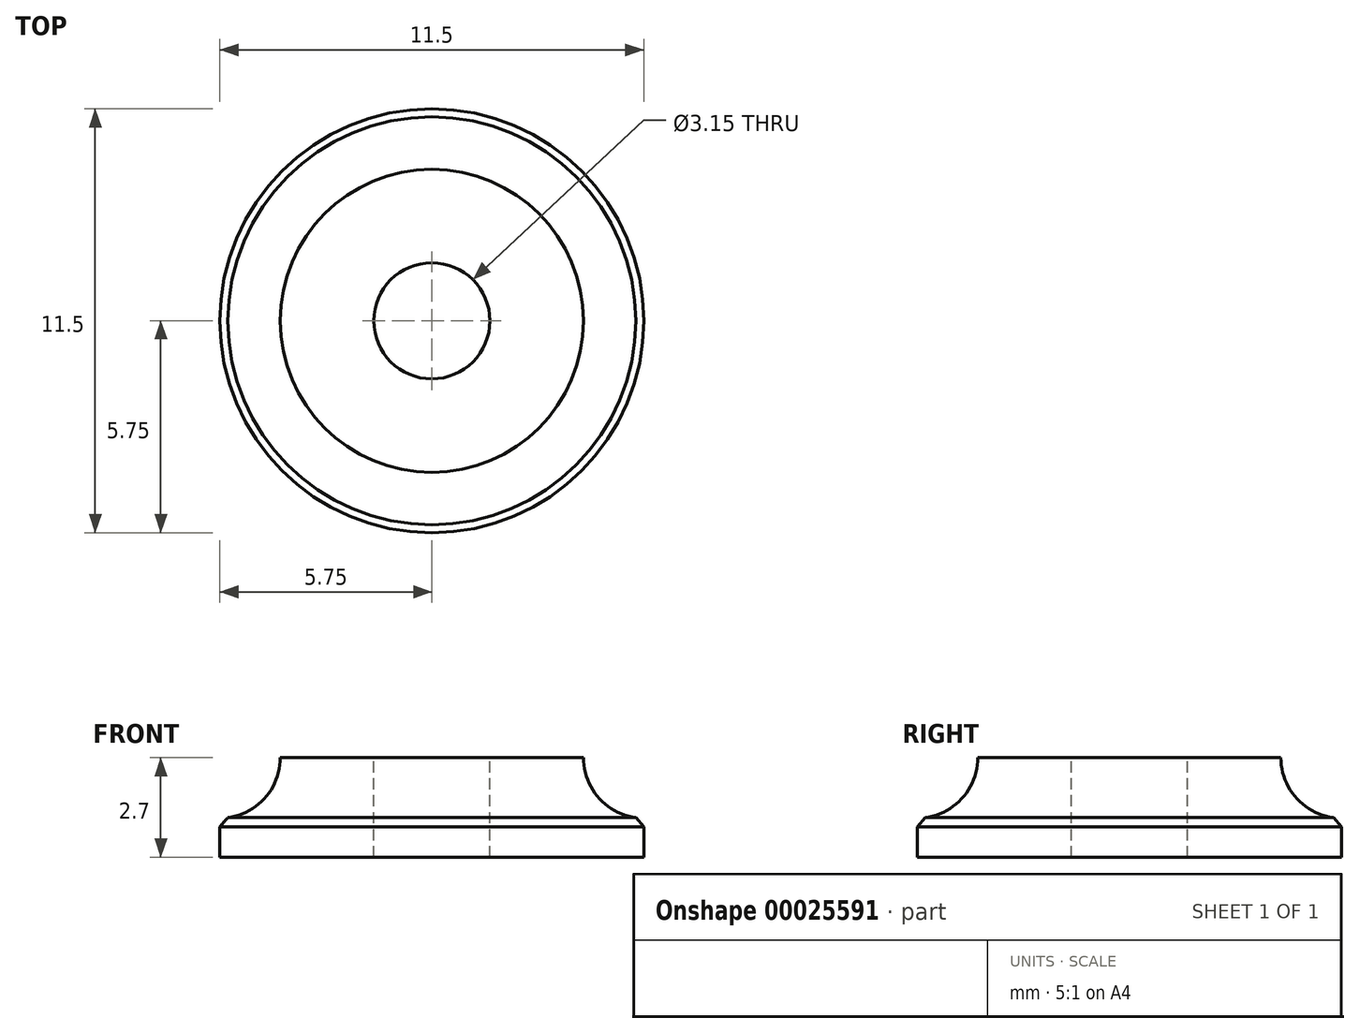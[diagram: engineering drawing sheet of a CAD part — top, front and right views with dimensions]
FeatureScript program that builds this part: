
annotation { "Feature Type Name" : "Feature", "Feature Type Description" : "" }
export const myFeature = defineFeature(function(context is Context, id is Id, definition is map)
    precondition{}
    {
        {
            var Q0;
            Q0=qCreatedBy(makeId("Front.planeOp"),FACE);
            var sketch = newSketch(context, id + "F0", { "sketchPlane" : qUnion([Q0])});
            skLineSegment(sketch, "E0", {"start": v(0, 0) * mm, "end": v(5.75, 0) * mm});
            skLineSegment(sketch, "E1", {"start": v(5.75, 0) * mm, "end": v(5.75, 1.06) * mm});
            skLineSegment(sketch, "E2", {"start": v(0, 0) * mm, "end": v(0, 2.7) * mm});
            skLineSegment(sketch, "E3", {"start": v(0, 2.7) * mm, "end": v(4.11, 2.7) * mm});
            skArc(sketch, "E4", {"start": v(4.11, 2.7) * mm, "mid": v(4.6, 1.54) * mm, "end": v(5.75, 1.06) * mm});
            skSolve(sketch);
        }
        {
            var Q0;
            Q0=makeQuery(id+"F0.imprint","IMPRINT",FACE,{"disambiguationData":[TD([[makeQuery(id+"F0.imprint","IMPRINT",EDGE,{"derivedFrom":sQuery(id+"F0.wireOp",EDGE,"E0")}),1.0]])]});
            var Q1;
            Q1=sQuery(id+"F0.wireOp",EDGE,"E2");
            revolve(context, id + "F1", {"entities" : qUnion([Q0]), "axis" : qUnion([Q1]), "revolveType" : RevolveType.FULL});
        }
        {
            var Q0;
            Q0=makeQuery(id+"F1.opRevolve","SWEPT_FACE",FACE,{"disambiguationData":[OSD([sQuery(id+"F0.wireOp",EDGE,"E3")])]});
            var sketch = newSketch(context, id + "F2", { "sketchPlane" : qUnion([Q0])});
            skCircle(sketch, "E5", {"center": v(0, 0) * mm, "radius": 1.57 * mm});
            skSolve(sketch);
        }
        {
            var Q0;
            Q0=makeQuery(id+"F2.imprint","IMPRINT",FACE,{"disambiguationData":[TD([[makeQuery(id+"F2.imprint","IMPRINT",EDGE,{"derivedFrom":sQuery(id+"F2.wireOp",EDGE,"E5")}),1.0]])]});
            extrude(context, id + "F3", {"entities" : qUnion([Q0]), "operationType" : NewBodyOperationType.REMOVE, "endBound" : BoundingType.UP_TO_NEXT, "oppositeDirection" : true, "depth" : 25 * mm});
        }
        {
            var Q0;
            Q0=makeQuery(id+"F1.opRevolve","SWEPT_EDGE",EDGE,{"disambiguationData":[OSD([sQuery(id+"F0.wireOp",EDGE,"E1"),sQuery(id+"F0.wireOp",EDGE,"E4")])]});
            chamfer(context, id + "F4", {"entities" : qUnion([Q0]), "width" : 0.25 * mm});
        }
    });
